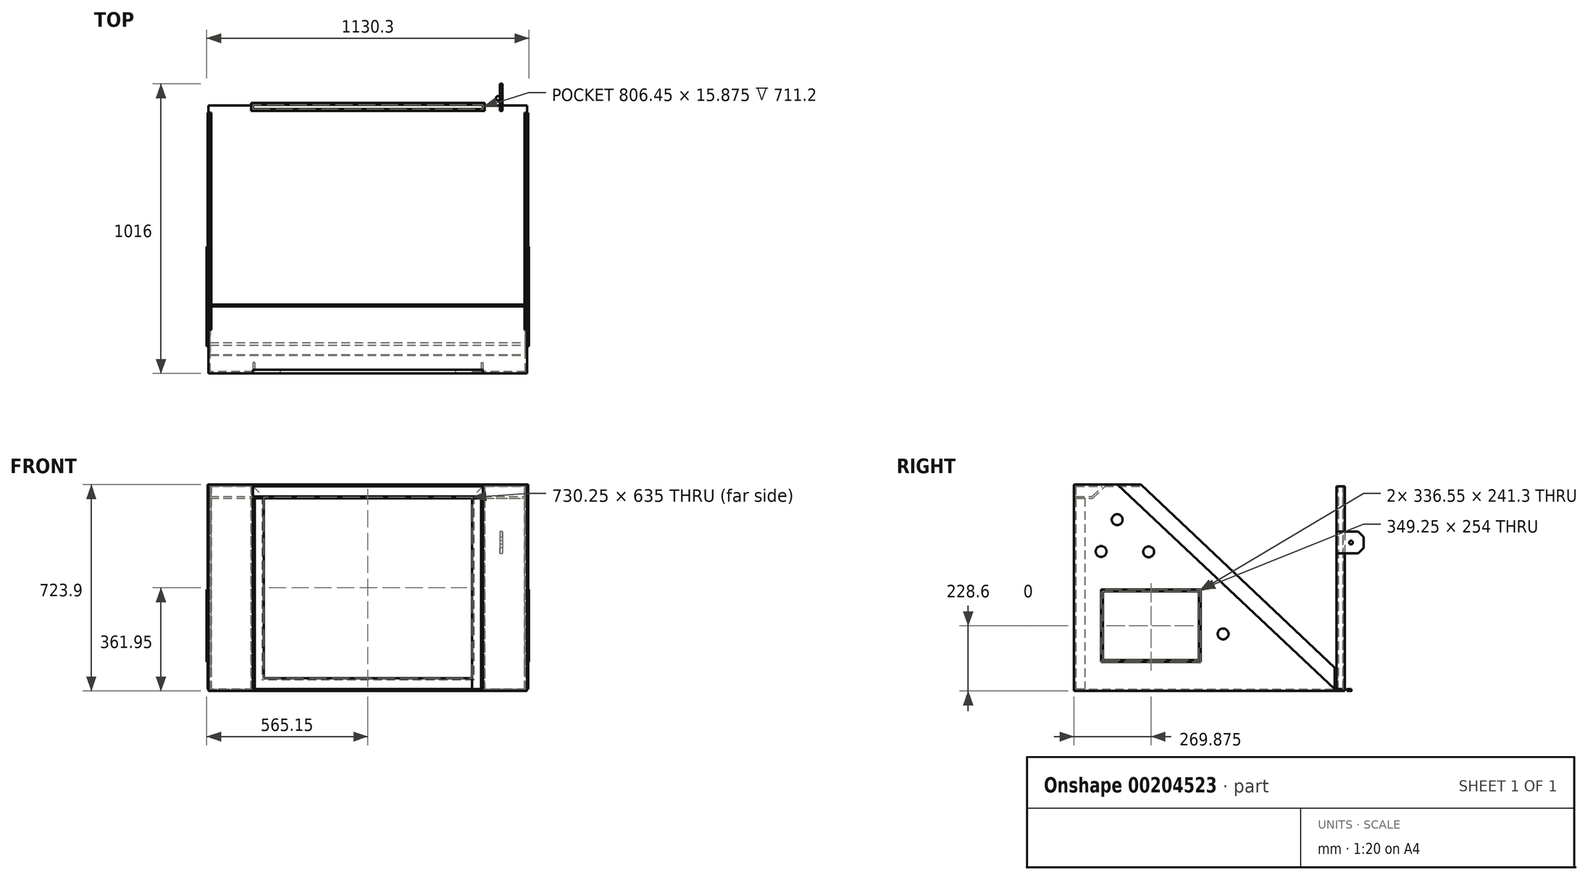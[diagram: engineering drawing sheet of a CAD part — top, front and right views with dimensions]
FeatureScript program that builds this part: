
annotation { "Feature Type Name" : "Feature", "Feature Type Description" : "" }
export const myFeature = defineFeature(function(context is Context, id is Id, definition is map)
    precondition{}
    {
        {
            var Q0;
            Q0=qCreatedBy(makeId("Front.planeOp"),FACE);
            var sketch = newSketch(context, id + "F0", { "sketchPlane" : qUnion([Q0])});
            skLineSegment(sketch, "E0", {"start": v(-558.8, 361.95) * mm, "end": v(-558.8, -361.95) * mm});
            skLineSegment(sketch, "E1", {"start": v(-558.8, -361.95) * mm, "end": v(558.8, -361.95) * mm});
            skLineSegment(sketch, "E2", {"start": v(558.8, -361.95) * mm, "end": v(558.8, 361.95) * mm});
            skLineSegment(sketch, "E3", {"start": v(-558.8, 361.95) * mm, "end": v(558.8, 361.95) * mm});
            skLineSegment(sketch, "E4", {"start": v(-403.23, -355.6) * mm, "end": v(-403.23, 355.6) * mm});
            skLineSegment(sketch, "E5", {"start": v(-403.23, 355.6) * mm, "end": v(403.22, 355.6) * mm});
            skLineSegment(sketch, "E6", {"start": v(403.22, 355.6) * mm, "end": v(403.22, -355.6) * mm});
            skLineSegment(sketch, "E7", {"start": v(-403.22, -355.6) * mm, "end": v(403.22, -355.6) * mm});
            skLineSegment(sketch, "E8", {"start": v(-552.45, 361.95) * mm, "end": v(-552.45, -361.95) * mm});
            skLineSegment(sketch, "E9", {"start": v(552.45, 361.95) * mm, "end": v(552.45, -361.95) * mm});
            skLineSegment(sketch, "E10", {"start": v(403.22, 355.6) * mm, "end": v(552.45, 355.6) * mm});
            skLineSegment(sketch, "E11", {"start": v(-403.23, 355.6) * mm, "end": v(-552.45, 355.6) * mm});
            skLineSegment(sketch, "E12", {"start": v(403.22, -355.6) * mm, "end": v(552.45, -355.6) * mm});
            skLineSegment(sketch, "E13", {"start": v(-403.23, -355.6) * mm, "end": v(-552.45, -355.6) * mm});
            skSolve(sketch);
        }
        {
            var Q0;
            Q0=makeQuery(id+"F0.imprint","IMPRINT",FACE,{"disambiguationData":[TD([[makeQuery(id+"F0.imprint","IMPRINT",EDGE,{"derivedFrom":sQuery(id+"F0.wireOp",EDGE,"E4")}),1.0]])]});
            var Q1;
            Q1=makeQuery(id+"F0.imprint","IMPRINT",FACE,{"disambiguationData":[TD([[makeQuery(id+"F0.imprint","IMPRINT",EDGE,{"derivedFrom":sQuery(id+"F0.wireOp",EDGE,"E6")}),1.0]])]});
            extrude(context, id + "F1", {"entities" : qUnion([Q0, Q1]), "depth" : 6.35 * mm});
        }
        {
            var Q0;
            {var subQ0=sQuery(id+"F0.wireOp",EDGE,"E0");Q0=makeQuery(id+"F0.imprint","IMPRINT",FACE,{"disambiguationData":[TD([[makeQuery(id+"F0.imprint","IMPRINT",EDGE,{"derivedFrom":subQ0}),1.0]])]});}
            var Q1;
            {var subQ0=sQuery(id+"F0.wireOp",EDGE,"E2");Q1=makeQuery(id+"F0.imprint","IMPRINT",FACE,{"disambiguationData":[TD([[makeQuery(id+"F0.imprint","IMPRINT",EDGE,{"derivedFrom":subQ0}),1.0]])]});}
            extrude(context, id + "F2", {"entities" : qUnion([Q0, Q1]), "operationType" : NewBodyOperationType.ADD, "depth" : 914.4 * mm});
        }
        {
            var Q0;
            Q0=makeQuery(id+"F0.imprint","IMPRINT",FACE,{"disambiguationData":[TD([[makeQuery(id+"F0.imprint","IMPRINT",EDGE,{"derivedFrom":sQuery(id+"F0.wireOp",EDGE,"E5")}),1.0]])]});
            var Q1;
            Q1=makeQuery(id+"F0.imprint","IMPRINT",FACE,{"disambiguationData":[TD([[makeQuery(id+"F0.imprint","IMPRINT",EDGE,{"derivedFrom":sQuery(id+"F0.wireOp",EDGE,"E7")}),-1.0]])]});
            extrude(context, id + "F3", {"entities" : qUnion([Q0, Q1]), "operationType" : NewBodyOperationType.ADD, "depth" : 914.4 * mm});
        }
        {
            var Q0;
            {var subQ0=sQuery(id+"F0.wireOp",EDGE,"E9");var subQ1=sQuery(id+"F0.wireOp",EDGE,"E8");var subQ2=sQuery(id+"F0.wireOp",EDGE,"E3");var subQ3=sQuery(id+"F0.wireOp",EDGE,"E1");Q0=makeQuery(id+"F3.boolean.opBoolean","MERGE",FACE,{"derivedFrom":[makeQuery(id+"F2.opExtrude","CAP_FACE",FACE,{"disambiguationData":[OSD([sQuery(id+"F0.wireOp",EDGE,"E0"),subQ3,subQ2,subQ1])],"isStart":false}),makeQuery(id+"F2.opExtrude","CAP_FACE",FACE,{"disambiguationData":[OSD([subQ3,sQuery(id+"F0.wireOp",EDGE,"E2"),subQ2,subQ0])],"isStart":false}),makeQuery(id+"F3.opExtrude","CAP_FACE",FACE,{"disambiguationData":[OSD([subQ3,sQuery(id+"F0.wireOp",EDGE,"E7"),subQ1,subQ0,sQuery(id+"F0.wireOp",EDGE,"E12"),sQuery(id+"F0.wireOp",EDGE,"E13")])],"isStart":false}),makeQuery(id+"F3.opExtrude","CAP_FACE",FACE,{"disambiguationData":[OSD([subQ2,sQuery(id+"F0.wireOp",EDGE,"E5"),subQ1,subQ0,sQuery(id+"F0.wireOp",EDGE,"E10"),sQuery(id+"F0.wireOp",EDGE,"E11")])],"isStart":false})]});}
            var sketch = newSketch(context, id + "F4", { "sketchPlane" : qUnion([Q0])});
            skLineSegment(sketch, "E14.bottom", {"start": v(-558.8, 361.95) * mm, "end": v(558.8, 361.95) * mm});
            skLineSegment(sketch, "E14.top", {"start": v(-558.8, -361.95) * mm, "end": v(558.8, -361.95) * mm});
            skLineSegment(sketch, "E14.left", {"start": v(-558.8, 361.95) * mm, "end": v(-558.8, -361.95) * mm});
            skLineSegment(sketch, "E14.right", {"start": v(558.8, 361.95) * mm, "end": v(558.8, -361.95) * mm});
            skSolve(sketch);
        }
        {
            var Q0;
            Q0=qSketchRegion(id+"F4",true);
            extrude(context, id + "F5", {"entities" : qUnion([Q0]), "operationType" : NewBodyOperationType.ADD, "depth" : 6.35 * mm});
        }
        {
            var Q0;
            Q0=makeQuery(id+"F5.boolean.opBoolean","MERGE",FACE,{"derivedFrom":[makeQuery(id+"F2.opExtrude","SWEPT_FACE",FACE,{"disambiguationData":[OSD([sQuery(id+"F0.wireOp",EDGE,"E2")])]}),makeQuery(id+"F5.opExtrude","SWEPT_FACE",FACE,{"disambiguationData":[OSD([sQuery(id+"F4.wireOp",EDGE,"E14.right")])]})]});
            var sketch = newSketch(context, id + "F6", { "sketchPlane" : qUnion([Q0])});
            skLineSegment(sketch, "E15.bottom", {"start": v(-825.5, -6.35) * mm, "end": v(-476.25, -6.35) * mm});
            skLineSegment(sketch, "E15.top", {"start": v(-825.5, -260.35) * mm, "end": v(-476.25, -260.35) * mm});
            skLineSegment(sketch, "E15.left", {"start": v(-825.5, -6.35) * mm, "end": v(-825.5, -260.35) * mm});
            skLineSegment(sketch, "E15.right", {"start": v(-476.25, -6.35) * mm, "end": v(-476.25, -260.35) * mm});
            skLineSegment(sketch, "E16.0", {"start": v(-819.15, -12.7) * mm, "end": v(-482.6, -12.7) * mm});
            skLineSegment(sketch, "E16.1", {"start": v(-819.15, -12.7) * mm, "end": v(-819.15, -254) * mm});
            skLineSegment(sketch, "E16.2", {"start": v(-819.15, -254) * mm, "end": v(-482.6, -254) * mm});
            skLineSegment(sketch, "E16.3", {"start": v(-482.6, -12.7) * mm, "end": v(-482.6, -254) * mm});
            skSolve(sketch);
        }
        {
            var Q0;
            Q0=makeQuery(id+"F6.imprint","IMPRINT",FACE,{"disambiguationData":[TD([[makeQuery(id+"F6.imprint","IMPRINT",EDGE,{"derivedFrom":sQuery(id+"F6.wireOp",EDGE,"E16.0")}),-1.0]])]});
            extrude(context, id + "F7", {"entities" : qUnion([Q0]), "operationType" : NewBodyOperationType.REMOVE, "oppositeDirection" : true, "depth" : 1270 * mm});
        }
        {
            var Q0;
            Q0=makeQuery(id+"F6.imprint","IMPRINT",FACE,{"disambiguationData":[TD([[makeQuery(id+"F6.imprint","IMPRINT",EDGE,{"derivedFrom":sQuery(id+"F6.wireOp",EDGE,"E15.bottom")}),-1.0]])]});
            extrude(context, id + "F8", {"entities" : qUnion([Q0]), "operationType" : NewBodyOperationType.ADD, "depth" : 6.35 * mm});
        }
        {
            var Q0;
            Q0=makeQuery(id+"F5.boolean.opBoolean","MERGE",FACE,{"derivedFrom":[makeQuery(id+"F2.opExtrude","SWEPT_FACE",FACE,{"disambiguationData":[OSD([sQuery(id+"F0.wireOp",EDGE,"E0")])]}),makeQuery(id+"F5.opExtrude","SWEPT_FACE",FACE,{"disambiguationData":[OSD([sQuery(id+"F4.wireOp",EDGE,"E14.left")])]})]});
            var sketch = newSketch(context, id + "F9", { "sketchPlane" : qUnion([Q0])});
            skLineSegment(sketch, "E17.0", {"start": v(825.5, -6.35) * mm, "end": v(476.25, -6.35) * mm});
            skLineSegment(sketch, "E17.1", {"start": v(825.5, -6.35) * mm, "end": v(825.5, -260.35) * mm});
            skLineSegment(sketch, "E17.2", {"start": v(825.5, -260.35) * mm, "end": v(476.25, -260.35) * mm});
            skLineSegment(sketch, "E17.3", {"start": v(476.25, -6.35) * mm, "end": v(476.25, -260.35) * mm});
            skSolve(sketch);
        }
        {
            var Q0;
            Q0=makeQuery(id+"F9.imprint","IMPRINT",FACE,{"disambiguationData":[TD([[makeQuery(id+"F9.imprint","IMPRINT",EDGE,{"derivedFrom":sQuery(id+"F9.wireOp",EDGE,"E17.0")}),1.0]])]});
            extrude(context, id + "F10", {"entities" : qUnion([Q0]), "operationType" : NewBodyOperationType.ADD, "depth" : 6.35 * mm});
        }
        {
            var Q0;
            Q0=makeQuery(id+"F5.boolean.opBoolean","MERGE",FACE,{"derivedFrom":[makeQuery(id+"F2.opExtrude","SWEPT_FACE",FACE,{"disambiguationData":[OSD([sQuery(id+"F0.wireOp",EDGE,"E0")])]}),makeQuery(id+"F5.opExtrude","SWEPT_FACE",FACE,{"disambiguationData":[OSD([sQuery(id+"F4.wireOp",EDGE,"E14.left")])]})]});
            var sketch = newSketch(context, id + "F11", { "sketchPlane" : qUnion([Q0])});
            skCircle(sketch, "E18.5.0.0", {"center": v(769.22, 239.06) * mm, "radius": 19.05 * mm});
            skCircle(sketch, "E19.3.0.0", {"center": v(658.89, 126.27) * mm, "radius": 19.05 * mm});
            skCircle(sketch, "E19.4.0.0", {"center": v(825.62, 127.5) * mm, "radius": 19.05 * mm});
            skCircle(sketch, "E20.MirrorC", {"center": v(397.76, -161.83) * mm, "radius": 19.05 * mm});
            skLineSegment(sketch, "E21", {"start": v(920.75, 361.95) * mm, "end": v(768.35, 361.95) * mm});
            skLineSegment(sketch, "E22", {"start": v(768.35, 361.95) * mm, "end": v(685.8, 361.95) * mm});
            skLineSegment(sketch, "E23", {"start": v(0, -361.95) * mm, "end": v(0, -285.75) * mm});
            skLineSegment(sketch, "E24", {"start": v(6.35, -279.75) * mm, "end": v(685.8, 361.95) * mm});
            skLineSegment(sketch, "E25", {"start": v(685.8, 361.95) * mm, "end": v(0, 361.95) * mm});
            skLineSegment(sketch, "E26", {"start": v(0, 361.95) * mm, "end": v(0, -285.75) * mm});
            skLineSegment(sketch, "E27", {"start": v(6.35, -361.95) * mm, "end": v(6.35, -279.75) * mm});
            skLineSegment(sketch, "E28", {"start": v(768.35, 361.95) * mm, "end": v(768.35, 336.55) * mm});
            skLineSegment(sketch, "E29", {"start": v(768.35, 336.55) * mm, "end": v(28.76, -361.95) * mm});
            skLineSegment(sketch, "E30", {"start": v(28.76, -361.95) * mm, "end": v(6.35, -361.95) * mm});
            skSolve(sketch);
        }
        {
            var Q0;
            Q0=sQuery(id+"F11.wireOp",VERTEX,"E18.direction1.start");
            var Q1;
            Q1=sQuery(id+"F11.wireOp",VERTEX,"E19.direction1.start");
            var Q2;
            Q2=sQuery(id+"F11.wireOp",VERTEX,"4a2ce049-4093-4add-8b6f-b7f52deebb400.MirrorC.center");
            var Q3;
            Q3=sQuery(id+"F11.wireOp",VERTEX,"a850cc24-eb14-4aa5-b13c-ffba9507b1460.MirrorC.center");
            var Q4;
            Q4=sQuery(id+"F11.wireOp",VERTEX,"E20.MirrorC.center");
            var Q5;
            Q5=sQuery(id+"F11.wireOp",VERTEX,"a32a4dfc-9795-497b-a0e1-e86128ed9b480.MirrorC.center");
            var Q6;
            Q6=sQuery(id+"F11.wireOp",VERTEX,"E19.direction1.end");
            var Q7;
            Q7=sQuery(id+"F11.wireOp",VERTEX,"E18.direction1.end");
            var Q8;
            Q8=sQuery(id+"F11.wireOp",VERTEX,"E18.2.0.0.center");
            var Q9;
            Q9=sQuery(id+"F11.wireOp",VERTEX,"E18.3.0.0.center");
            var Q10;
            Q10=sQuery(id+"F11.wireOp",VERTEX,"E19.3.0.0.center");
            var Q11;
            Q11=sQuery(id+"F11.wireOp",VERTEX,"E19.2.0.0.center");
            var Q12;
            Q12=sQuery(id+"F11.wireOp",VERTEX,"E18.4.0.0.center");
            var Q13;
            Q13=sQuery(id+"F11.wireOp",VERTEX,"E19.4.0.0.center");
            var Q14;
            Q14=sQuery(id+"F11.wireOp",VERTEX,"E18.5.0.0.center");
            var Q15;
            Q15=makeQuery(id+"F1.opExtrude","SWEPT_BODY",BODY,{"disambiguationData":[OSD([sQuery(id+"F0.wireOp",EDGE,"E4"),sQuery(id+"F0.wireOp",EDGE,"E8"),sQuery(id+"F0.wireOp",EDGE,"E11"),sQuery(id+"F0.wireOp",EDGE,"E13")])]});
            hole(context, id + "F12", {"style" : HoleStyle.SIMPLE, "endStyle" : HoleEndStyle.BLIND, "holeDiameter" : 38.1 * mm, "holeDepth" : 1524 * mm, "locations" : qUnion([Q0, Q1, Q2, Q3, Q4, Q5, Q6, Q7, Q8, Q9, Q10, Q11, Q12, Q13, Q14]), "scope" : qUnion([Q15])});
        }
        {
            var Q0;
            {var subQ0=sQuery(id+"F0.wireOp",EDGE,"E3");Q0=makeQuery(id+"F5.boolean.opBoolean","MERGE",FACE,{"derivedFrom":[makeQuery(id+"F3.boolean.opBoolean","MERGE",FACE,{"derivedFrom":[makeQuery(id+"F2.opExtrude","SWEPT_FACE",FACE,{"disambiguationData":[OSD([subQ0]),TDD([makeQuery(id+"F0.imprint","IMPRINT",EDGE,{"disambiguationData":[TD([[makeQuery(id+"F0.imprint","INTERSECT",VERTEX,{"derivedFrom":[sQuery(id+"F0.wireOp",EDGE,"E0"),subQ0]}),-1.0]])],"derivedFrom":subQ0})])]}),makeQuery(id+"F2.opExtrude","SWEPT_FACE",FACE,{"disambiguationData":[OSD([subQ0]),TDD([makeQuery(id+"F0.imprint","IMPRINT",EDGE,{"disambiguationData":[TD([[makeQuery(id+"F0.imprint","INTERSECT",VERTEX,{"derivedFrom":[sQuery(id+"F0.wireOp",EDGE,"E2"),subQ0]}),1.0]])],"derivedFrom":subQ0})])]}),makeQuery(id+"F3.opExtrude","SWEPT_FACE",FACE,{"disambiguationData":[OSD([subQ0])]})]}),makeQuery(id+"F5.opExtrude","SWEPT_FACE",FACE,{"disambiguationData":[OSD([sQuery(id+"F4.wireOp",EDGE,"E14.bottom")])]})]});}
            var sketch = newSketch(context, id + "F13", { "sketchPlane" : qUnion([Q0])});
            skLineSegment(sketch, "E31", {"start": v(188.2, -141.31) * mm, "end": v(366, -141.31) * mm});
            skLineSegment(sketch, "E32", {"start": v(366, -141.31) * mm, "end": v(366, -382.61) * mm});
            skLineSegment(sketch, "E33", {"start": v(366, -382.61) * mm, "end": v(188.2, -382.61) * mm});
            skLineSegment(sketch, "E34", {"start": v(188.2, -382.61) * mm, "end": v(188.2, -141.31) * mm});
            skSolve(sketch);
        }
        {
            var Q0;
            Q0=makeQuery(id+"F13.imprint","IMPRINT",FACE,{"disambiguationData":[TD([[makeQuery(id+"F13.imprint","IMPRINT",EDGE,{"derivedFrom":sQuery(id+"F13.wireOp",EDGE,"E31")}),-1.0]])]});
            extrude(context, id + "F14", {"entities" : qUnion([Q0]), "operationType" : NewBodyOperationType.REMOVE, "oppositeDirection" : true, "depth" : 25.4 * mm});
        }
        {
            var Q0;
            Q0=makeQuery(id+"F0.imprint","IMPRINT",FACE,{"disambiguationData":[TD([[makeQuery(id+"F0.imprint","IMPRINT",EDGE,{"derivedFrom":sQuery(id+"F0.wireOp",EDGE,"E6")}),1.0]])]});
            var sketch = newSketch(context, id + "F15", { "sketchPlane" : qUnion([Q0])});
            skLineSegment(sketch, "E35.bottom", {"start": v(472.25, 196.85) * mm, "end": v(462.72, 196.85) * mm});
            skLineSegment(sketch, "E35.top", {"start": v(472.25, 120.65) * mm, "end": v(462.72, 120.65) * mm});
            skLineSegment(sketch, "E35.left", {"start": v(472.25, 196.85) * mm, "end": v(472.25, 120.65) * mm});
            skLineSegment(sketch, "E35.right", {"start": v(462.72, 196.85) * mm, "end": v(462.72, 120.65) * mm});
            skSolve(sketch);
        }
        {
            var Q0;
            Q0=qSketchRegion(id+"F15",true);
            extrude(context, id + "F16", {"entities" : qUnion([Q0]), "operationType" : NewBodyOperationType.ADD, "oppositeDirection" : true, "depth" : 95.25 * mm});
        }
        {
            var Q0;
            Q0=makeQuery(id+"F16.opExtrude","CAP_EDGE",EDGE,{"disambiguationData":[OSD([sQuery(id+"F15.wireOp",EDGE,"E35.top")])],"isStart":false});
            var Q1;
            Q1=makeQuery(id+"F16.opExtrude","CAP_EDGE",EDGE,{"disambiguationData":[OSD([sQuery(id+"F15.wireOp",EDGE,"E35.bottom")])],"isStart":false});
            chamfer(context, id + "F17", {"entities" : qUnion([Q0, Q1]), "width" : 19.05 * mm, "tangentPropagation" : true});
        }
        {
            var Q0;
            Q0=makeQuery(id+"F16.opExtrude","SWEPT_FACE",FACE,{"disambiguationData":[OSD([sQuery(id+"F15.wireOp",EDGE,"E35.right")])]});
            var sketch = newSketch(context, id + "F18", { "sketchPlane" : qUnion([Q0])});
            skLineSegment(sketch, "E36", {"start": v(-50.8, 120.65) * mm, "end": v(-50.8, 158.75) * mm});
            skSolve(sketch);
        }
        {
            var Q0;
            Q0=sQuery(id+"F18.wireOp",VERTEX,"E36.end");
            var Q1;
            Q1=makeQuery(id+"F1.opExtrude","SWEPT_BODY",BODY,{"disambiguationData":[OSD([sQuery(id+"F0.wireOp",EDGE,"E4"),sQuery(id+"F0.wireOp",EDGE,"E8"),sQuery(id+"F0.wireOp",EDGE,"E11"),sQuery(id+"F0.wireOp",EDGE,"E13")])]});
            hole(context, id + "F19", {"style" : HoleStyle.SIMPLE, "endStyle" : HoleEndStyle.BLIND, "holeDiameter" : 12.7 * mm, "holeDepth" : 1524 * mm, "locations" : qUnion([Q0]), "scope" : qUnion([Q1])});
        }
        {
            var Q0;
            Q0=makeQuery(id+"F0.imprint","IMPRINT",FACE,{"disambiguationData":[TD([[makeQuery(id+"F0.imprint","IMPRINT",EDGE,{"derivedFrom":sQuery(id+"F0.wireOp",EDGE,"E4")}),-1.0]])]});
            extrude(context, id + "F20", {"entities" : qUnion([Q0]), "operationType" : NewBodyOperationType.REMOVE, "depth" : 1270 * mm});
        }
        {
            var Q0;
            Q0=makeQuery(id+"F0.imprint","IMPRINT",FACE,{"disambiguationData":[TD([[makeQuery(id+"F0.imprint","IMPRINT",EDGE,{"derivedFrom":sQuery(id+"F0.wireOp",EDGE,"E4")}),-1.0]])]});
            var sketch = newSketch(context, id + "F21", { "sketchPlane" : qUnion([Q0])});
            skLineSegment(sketch, "E37", {"start": v(403.23, 355.6) * mm, "end": v(403.23, -355.6) * mm});
            skLineSegment(sketch, "E38.0", {"start": v(365.13, 317.5) * mm, "end": v(365.13, -317.5) * mm});
            skLineSegment(sketch, "E39", {"start": v(403.23, 355.6) * mm, "end": v(365.13, 317.5) * mm});
            skLineSegment(sketch, "E40", {"start": v(403.23, -355.6) * mm, "end": v(365.13, -317.5) * mm});
            skLineSegment(sketch, "E41.0", {"start": v(396.88, 349.25) * mm, "end": v(396.88, -349.25) * mm});
            skLineSegment(sketch, "E42.MirrorCS", {"start": v(-365.13, 317.5) * mm, "end": v(-365.13, -317.5) * mm});
            skLineSegment(sketch, "E43.MirrorCS", {"start": v(-396.88, 349.25) * mm, "end": v(-396.88, -349.25) * mm});
            skLineSegment(sketch, "E44.MirrorCS", {"start": v(-403.23, 355.6) * mm, "end": v(-403.23, -355.6) * mm});
            skLineSegment(sketch, "E45.MirrorCS", {"start": v(-403.23, 355.6) * mm, "end": v(-365.13, 317.5) * mm});
            skLineSegment(sketch, "E46.MirrorCS", {"start": v(-403.23, -355.6) * mm, "end": v(-365.13, -317.5) * mm});
            skLineSegment(sketch, "E47", {"start": v(403.23, 355.6) * mm, "end": v(-403.23, 355.6) * mm});
            skLineSegment(sketch, "E48", {"start": v(365.13, 317.5) * mm, "end": v(-365.13, 317.5) * mm});
            skLineSegment(sketch, "E49", {"start": v(-396.88, 349.25) * mm, "end": v(396.88, 349.25) * mm});
            skLineSegment(sketch, "E50.MirrorCS", {"start": v(365.13, -317.5) * mm, "end": v(-365.13, -317.5) * mm});
            skLineSegment(sketch, "E51.MirrorCS", {"start": v(-396.88, -349.25) * mm, "end": v(396.88, -349.25) * mm});
            skLineSegment(sketch, "E52.MirrorCS", {"start": v(403.23, -355.6) * mm, "end": v(-403.23, -355.6) * mm});
            skSolve(sketch);
        }
        {
            var Q0;
            {var subQ0=sQuery(id+"F21.wireOp",EDGE,"E42.MirrorCS");Q0=makeQuery(id+"F21.imprint","IMPRINT",FACE,{"disambiguationData":[TD([[makeQuery(id+"F21.imprint","IMPRINT",EDGE,{"derivedFrom":subQ0}),-1.0]])]});}
            var Q1;
            {var subQ0=sQuery(id+"F21.wireOp",EDGE,"E48");Q1=makeQuery(id+"F21.imprint","IMPRINT",FACE,{"disambiguationData":[TD([[makeQuery(id+"F21.imprint","IMPRINT",EDGE,{"derivedFrom":subQ0}),-1.0]])]});}
            var Q2;
            {var subQ0=sQuery(id+"F21.wireOp",EDGE,"E50.MirrorCS");Q2=makeQuery(id+"F21.imprint","IMPRINT",FACE,{"disambiguationData":[TD([[makeQuery(id+"F21.imprint","IMPRINT",EDGE,{"derivedFrom":subQ0}),1.0]])]});}
            var Q3;
            {var subQ0=sQuery(id+"F21.wireOp",EDGE,"E38.0");Q3=makeQuery(id+"F21.imprint","IMPRINT",FACE,{"disambiguationData":[TD([[makeQuery(id+"F21.imprint","IMPRINT",EDGE,{"derivedFrom":subQ0}),1.0]])]});}
            extrude(context, id + "F22", {"entities" : qUnion([Q0, Q1, Q2, Q3]), "oppositeDirection" : true, "depth" : 6.35 * mm});
        }
        {
            var Q0;
            {var subQ0=sQuery(id+"F21.wireOp",EDGE,"E47");Q0=makeQuery(id+"F21.imprint","IMPRINT",FACE,{"disambiguationData":[TD([[makeQuery(id+"F21.imprint","IMPRINT",EDGE,{"derivedFrom":subQ0}),-1.0]])]});}
            var Q1;
            {var subQ0=sQuery(id+"F21.wireOp",EDGE,"E37");Q1=makeQuery(id+"F21.imprint","IMPRINT",FACE,{"disambiguationData":[TD([[makeQuery(id+"F21.imprint","IMPRINT",EDGE,{"derivedFrom":subQ0}),-1.0]])]});}
            var Q2;
            {var subQ2=sQuery(id+"F21.wireOp",EDGE,"E51.MirrorCS");Q2=makeQuery(id+"F21.imprint","IMPRINT",FACE,{"disambiguationData":[TD([[makeQuery(id+"F21.imprint","IMPRINT",EDGE,{"derivedFrom":subQ2}),-1.0]])]});}
            var Q3;
            {var subQ0=sQuery(id+"F21.wireOp",EDGE,"E43.MirrorCS");Q3=makeQuery(id+"F21.imprint","IMPRINT",FACE,{"disambiguationData":[TD([[makeQuery(id+"F21.imprint","IMPRINT",EDGE,{"derivedFrom":subQ0}),-1.0]])]});}
            var Q4;
            Q4=makeQuery(id+"F22.opExtrude","CAP_FACE",FACE,{"disambiguationData":[OSD([sQuery(id+"F21.wireOp",EDGE,"E38.0"),sQuery(id+"F21.wireOp",EDGE,"E41.0"),sQuery(id+"F21.wireOp",EDGE,"E42.MirrorCS"),sQuery(id+"F21.wireOp",EDGE,"E43.MirrorCS"),sQuery(id+"F21.wireOp",EDGE,"E48"),sQuery(id+"F21.wireOp",EDGE,"E49"),sQuery(id+"F21.wireOp",EDGE,"E50.MirrorCS"),sQuery(id+"F21.wireOp",EDGE,"E51.MirrorCS")])],"isStart":false});
            extrude(context, id + "F23", {"entities" : qUnion([Q0, Q1, Q2, Q3]), "depth" : 25.4 * mm, "hasSecondDirection" : true, "secondDirectionBound" : SecondDirectionBoundingType.UP_TO_SURFACE, "secondDirectionOppositeDirection" : true, "secondDirectionBoundEntityFace" : qUnion([Q4]), "secondDirectionDepth" : 25.4 * mm});
        }
        {
            var Q0;
            Q0=makeQuery(id+"F22.opExtrude","SWEPT_BODY",BODY,{"disambiguationData":[OSD([sQuery(id+"F21.wireOp",EDGE,"E38.0"),sQuery(id+"F21.wireOp",EDGE,"E41.0"),sQuery(id+"F21.wireOp",EDGE,"E42.MirrorCS"),sQuery(id+"F21.wireOp",EDGE,"E43.MirrorCS"),sQuery(id+"F21.wireOp",EDGE,"E48"),sQuery(id+"F21.wireOp",EDGE,"E49"),sQuery(id+"F21.wireOp",EDGE,"E50.MirrorCS"),sQuery(id+"F21.wireOp",EDGE,"E51.MirrorCS")])]});
            var Q1;
            Q1=makeQuery(id+"F23.opExtrude","SWEPT_BODY",BODY,{"disambiguationData":[OSD([sQuery(id+"F21.wireOp",EDGE,"E37"),sQuery(id+"F21.wireOp",EDGE,"E41.0"),sQuery(id+"F21.wireOp",EDGE,"E43.MirrorCS"),sQuery(id+"F21.wireOp",EDGE,"E44.MirrorCS"),sQuery(id+"F21.wireOp",EDGE,"E47"),sQuery(id+"F21.wireOp",EDGE,"E49"),sQuery(id+"F21.wireOp",EDGE,"E51.MirrorCS"),sQuery(id+"F21.wireOp",EDGE,"E52.MirrorCS")])]});
            var Q2;
            Q2=makeQuery(id+"F1.opExtrude","SWEPT_BODY",BODY,{"disambiguationData":[OSD([sQuery(id+"F0.wireOp",EDGE,"E4"),sQuery(id+"F0.wireOp",EDGE,"E8"),sQuery(id+"F0.wireOp",EDGE,"E11"),sQuery(id+"F0.wireOp",EDGE,"E13")])]});
            booleanBodies(context, id + "F24", {"operationType" : BooleanOperationType.UNION, "tools" : qUnion([Q0, Q1, Q2])});
        }
        {
            var Q0;
            {var subQ0=sQuery(id+"F21.wireOp",EDGE,"E51.MirrorCS");var subQ1=sQuery(id+"F21.wireOp",EDGE,"E49");var subQ2=sQuery(id+"F21.wireOp",EDGE,"E43.MirrorCS");var subQ3=sQuery(id+"F21.wireOp",EDGE,"E41.0");Q0=makeQuery(id+"F24.opBoolean","MERGE",FACE,{"derivedFrom":[makeQuery(id+"F22.opExtrude","CAP_FACE",FACE,{"disambiguationData":[OSD([sQuery(id+"F21.wireOp",EDGE,"E38.0"),subQ3,sQuery(id+"F21.wireOp",EDGE,"E42.MirrorCS"),subQ2,sQuery(id+"F21.wireOp",EDGE,"E48"),subQ1,sQuery(id+"F21.wireOp",EDGE,"E50.MirrorCS"),subQ0])],"isStart":false}),makeQuery(id+"F23.opExtrude","CAP_FACE",FACE,{"disambiguationData":[OSD([sQuery(id+"F21.wireOp",EDGE,"E37"),subQ3,subQ2,sQuery(id+"F21.wireOp",EDGE,"E44.MirrorCS"),sQuery(id+"F21.wireOp",EDGE,"E47"),subQ1,subQ0,sQuery(id+"F21.wireOp",EDGE,"E52.MirrorCS")])],"isStart":true})]});}
            var sketch = newSketch(context, id + "F25", { "sketchPlane" : qUnion([Q0])});
            skLineSegment(sketch, "E53.0", {"start": v(371.48, 324.21) * mm, "end": v(371.48, -323.85) * mm});
            skLineSegment(sketch, "E53.1", {"start": v(-371.48, -323.85) * mm, "end": v(371.48, -323.85) * mm});
            skLineSegment(sketch, "E53.2", {"start": v(-371.48, 324.21) * mm, "end": v(-371.48, -323.85) * mm});
            skLineSegment(sketch, "E54.MirrorCS", {"start": v(403.22, 355.6) * mm, "end": v(371.48, 324.21) * mm});
            skLineSegment(sketch, "E55.0", {"start": v(403.23, 355.6) * mm, "end": v(403.23, -355.6) * mm});
            skLineSegment(sketch, "E55.1", {"start": v(-403.23, -355.6) * mm, "end": v(403.23, -355.6) * mm});
            skLineSegment(sketch, "E55.2", {"start": v(-403.23, 355.64) * mm, "end": v(-403.23, -355.6) * mm});
            skLineSegment(sketch, "E56", {"start": v(-403.23, 355.64) * mm, "end": v(-371.48, 324.21) * mm});
            skLineSegment(sketch, "E57.0", {"start": v(409.58, 355.6) * mm, "end": v(409.58, -361.95) * mm});
            skLineSegment(sketch, "E57.1", {"start": v(-409.58, -361.95) * mm, "end": v(409.58, -361.95) * mm});
            skLineSegment(sketch, "E57.2", {"start": v(-409.58, 355.6) * mm, "end": v(-409.58, -361.95) * mm});
            skLineSegment(sketch, "E58", {"start": v(-403.23, 355.64) * mm, "end": v(-409.58, 355.6) * mm});
            skLineSegment(sketch, "E59", {"start": v(403.22, 355.6) * mm, "end": v(409.58, 355.6) * mm});
            skSolve(sketch);
        }
        {
            var Q0;
            Q0=makeQuery(id+"F25.imprint","IMPRINT",FACE,{"disambiguationData":[TD([[makeQuery(id+"F25.imprint","IMPRINT",EDGE,{"derivedFrom":sQuery(id+"F25.wireOp",EDGE,"E53.0")}),1.0]])]});
            extrude(context, id + "F26", {"entities" : qUnion([Q0]), "depth" : 22.22 * mm, "hasSecondDirection" : true, "secondDirectionOppositeDirection" : false, "secondDirectionDepth" : 15.88 * mm});
        }
        {
            var Q0;
            Q0=makeQuery(id+"F25.imprint","IMPRINT",FACE,{"disambiguationData":[TD([[makeQuery(id+"F25.imprint","IMPRINT",EDGE,{"derivedFrom":sQuery(id+"F25.wireOp",EDGE,"E55.0")}),-1.0]])]});
            var Q1;
            Q1=makeQuery(id+"F26.opExtrude","CAP_FACE",FACE,{"disambiguationData":[OSD([sQuery(id+"F21.wireOp",EDGE,"E38.0"),sQuery(id+"F21.wireOp",EDGE,"E41.0"),sQuery(id+"F21.wireOp",EDGE,"E42.MirrorCS"),sQuery(id+"F21.wireOp",EDGE,"E43.MirrorCS"),sQuery(id+"F21.wireOp",EDGE,"E47"),sQuery(id+"F21.wireOp",EDGE,"E48"),sQuery(id+"F21.wireOp",EDGE,"E49"),sQuery(id+"F21.wireOp",EDGE,"E50.MirrorCS"),sQuery(id+"F21.wireOp",EDGE,"E51.MirrorCS"),sQuery(id+"F25.wireOp",EDGE,"E53.0"),sQuery(id+"F25.wireOp",EDGE,"E53.1"),sQuery(id+"F25.wireOp",EDGE,"E53.2"),sQuery(id+"F25.wireOp",EDGE,"E54.MirrorCS"),sQuery(id+"F25.wireOp",EDGE,"E55.0"),sQuery(id+"F25.wireOp",EDGE,"E55.1"),sQuery(id+"F25.wireOp",EDGE,"E55.2"),sQuery(id+"F25.wireOp",EDGE,"E56")])],"isStart":false});
            var Q2;
            {var subQ0=sQuery(id+"F0.wireOp",EDGE,"E11");var subQ1=sQuery(id+"F0.wireOp",EDGE,"E10");var subQ2=sQuery(id+"F0.wireOp",EDGE,"E9");var subQ3=sQuery(id+"F0.wireOp",EDGE,"E8");var subQ4=sQuery(id+"F0.wireOp",EDGE,"E3");var subQ5=sQuery(id+"F0.wireOp",EDGE,"E13");var subQ6=sQuery(id+"F0.wireOp",EDGE,"E12");var subQ7=sQuery(id+"F0.wireOp",EDGE,"E1");Q2=makeQuery(id+"F3.boolean.opBoolean","MERGE",FACE,{"derivedFrom":[makeQuery(id+"F2.boolean.opBoolean","MERGE",FACE,{"derivedFrom":[makeQuery(id+"F1.opExtrude","CAP_FACE",FACE,{"disambiguationData":[OSD([sQuery(id+"F0.wireOp",EDGE,"E4"),subQ3,subQ0,subQ5])],"isStart":true}),makeQuery(id+"F2.opExtrude","CAP_FACE",FACE,{"disambiguationData":[OSD([sQuery(id+"F0.wireOp",EDGE,"E0"),subQ7,subQ4,subQ3])],"isStart":true})]}),makeQuery(id+"F2.boolean.opBoolean","MERGE",FACE,{"derivedFrom":[makeQuery(id+"F1.opExtrude","CAP_FACE",FACE,{"disambiguationData":[OSD([sQuery(id+"F0.wireOp",EDGE,"E6"),subQ2,subQ1,subQ6])],"isStart":true}),makeQuery(id+"F2.opExtrude","CAP_FACE",FACE,{"disambiguationData":[OSD([subQ7,sQuery(id+"F0.wireOp",EDGE,"E2"),subQ4,subQ2])],"isStart":true})]}),makeQuery(id+"F3.opExtrude","CAP_FACE",FACE,{"disambiguationData":[OSD([subQ7,sQuery(id+"F0.wireOp",EDGE,"E7"),subQ3,subQ2,subQ6,subQ5])],"isStart":true}),makeQuery(id+"F3.opExtrude","CAP_FACE",FACE,{"disambiguationData":[OSD([subQ4,sQuery(id+"F0.wireOp",EDGE,"E5"),subQ3,subQ2,subQ1,subQ0])],"isStart":true})]});}
            extrude(context, id + "F27", {"entities" : qUnion([Q0]), "operationType" : NewBodyOperationType.ADD, "endBound" : BoundingType.UP_TO_SURFACE, "endBoundEntityFace" : qUnion([Q1]), "depth" : 25.4 * mm, "hasSecondDirection" : true, "secondDirectionBound" : SecondDirectionBoundingType.UP_TO_SURFACE, "secondDirectionOppositeDirection" : true, "secondDirectionBoundEntityFace" : qUnion([Q2]), "secondDirectionDepth" : 25.4 * mm});
        }
        {
            var Q0;
            {var subQ0=sQuery(id+"F0.wireOp",EDGE,"E1");Q0=makeQuery(id+"F5.boolean.opBoolean","MERGE",FACE,{"derivedFrom":[makeQuery(id+"F3.boolean.opBoolean","MERGE",FACE,{"derivedFrom":[makeQuery(id+"F2.opExtrude","SWEPT_FACE",FACE,{"disambiguationData":[OSD([subQ0]),TDD([makeQuery(id+"F0.imprint","IMPRINT",EDGE,{"disambiguationData":[TD([[makeQuery(id+"F0.imprint","INTERSECT",VERTEX,{"derivedFrom":[sQuery(id+"F0.wireOp",EDGE,"E0"),subQ0]}),-1.0]])],"derivedFrom":subQ0})])]}),makeQuery(id+"F2.opExtrude","SWEPT_FACE",FACE,{"disambiguationData":[OSD([subQ0]),TDD([makeQuery(id+"F0.imprint","IMPRINT",EDGE,{"disambiguationData":[TD([[makeQuery(id+"F0.imprint","INTERSECT",VERTEX,{"derivedFrom":[subQ0,sQuery(id+"F0.wireOp",EDGE,"E2")]}),1.0]])],"derivedFrom":subQ0})])]}),makeQuery(id+"F3.opExtrude","SWEPT_FACE",FACE,{"disambiguationData":[OSD([subQ0])]})]}),makeQuery(id+"F5.opExtrude","SWEPT_FACE",FACE,{"disambiguationData":[OSD([sQuery(id+"F4.wireOp",EDGE,"E14.top")])]})]});}
            var sketch = newSketch(context, id + "F28", { "sketchPlane" : qUnion([Q0])});
            skLineSegment(sketch, "E60", {"start": v(0, 920.75) * mm, "end": v(0, 908.05) * mm});
            skPoint(sketch, "E60.endSnap0", {"position": v(0, 920.75) * mm});
            skLineSegment(sketch, "E61", {"start": v(0, 908.05) * mm, "end": v(-307.98, 908.05) * mm});
            skLineSegment(sketch, "E62", {"start": v(-307.98, 908.05) * mm, "end": v(-307.98, 920.75) * mm});
            skLineSegment(sketch, "E63", {"start": v(-307.98, 920.75) * mm, "end": v(307.98, 920.75) * mm});
            skLineSegment(sketch, "E64", {"start": v(307.98, 920.75) * mm, "end": v(307.98, 908.05) * mm});
            skLineSegment(sketch, "E65", {"start": v(307.98, 908.05) * mm, "end": v(0, 908.05) * mm});
            skSolve(sketch);
        }
        {
            var Q0;
            Q0=qSketchRegion(id+"F28",true);
            extrude(context, id + "F29", {"entities" : qUnion([Q0]), "operationType" : NewBodyOperationType.REMOVE, "oppositeDirection" : true, "depth" : 1524 * mm});
        }
        {
            var Q0;
            {var subQ0=sQuery(id+"F0.wireOp",EDGE,"E3");Q0=makeQuery(id+"F5.boolean.opBoolean","MERGE",FACE,{"derivedFrom":[makeQuery(id+"F3.boolean.opBoolean","MERGE",FACE,{"derivedFrom":[makeQuery(id+"F2.opExtrude","SWEPT_FACE",FACE,{"disambiguationData":[OSD([subQ0]),TDD([makeQuery(id+"F0.imprint","IMPRINT",EDGE,{"disambiguationData":[TD([[makeQuery(id+"F0.imprint","INTERSECT",VERTEX,{"derivedFrom":[sQuery(id+"F0.wireOp",EDGE,"E0"),subQ0]}),-1.0]])],"derivedFrom":subQ0})])]}),makeQuery(id+"F2.opExtrude","SWEPT_FACE",FACE,{"disambiguationData":[OSD([subQ0]),TDD([makeQuery(id+"F0.imprint","IMPRINT",EDGE,{"disambiguationData":[TD([[makeQuery(id+"F0.imprint","INTERSECT",VERTEX,{"derivedFrom":[sQuery(id+"F0.wireOp",EDGE,"E2"),subQ0]}),1.0]])],"derivedFrom":subQ0})])]}),makeQuery(id+"F3.opExtrude","SWEPT_FACE",FACE,{"disambiguationData":[OSD([subQ0])]})]}),makeQuery(id+"F5.opExtrude","SWEPT_FACE",FACE,{"disambiguationData":[OSD([sQuery(id+"F4.wireOp",EDGE,"E14.bottom")])]})]});}
            var sketch = newSketch(context, id + "F30", { "sketchPlane" : qUnion([Q0])});
            skLineSegment(sketch, "E66", {"start": v(-307.98, -920.75) * mm, "end": v(-403.22, -920.75) * mm});
            skLineSegment(sketch, "E67", {"start": v(-403.22, -920.75) * mm, "end": v(-403.22, -908.05) * mm});
            skLineSegment(sketch, "E68", {"start": v(-403.22, -908.05) * mm, "end": v(-307.97, -908.05) * mm});
            skLineSegment(sketch, "E69", {"start": v(-307.97, -908.05) * mm, "end": v(-307.97, -920.75) * mm});
            skLineSegment(sketch, "E70", {"start": v(307.98, -908.05) * mm, "end": v(403.23, -908.05) * mm});
            skLineSegment(sketch, "E71", {"start": v(403.23, -908.05) * mm, "end": v(403.23, -920.75) * mm});
            skLineSegment(sketch, "E72", {"start": v(403.23, -920.75) * mm, "end": v(307.98, -920.75) * mm});
            skLineSegment(sketch, "E73", {"start": v(307.98, -920.75) * mm, "end": v(307.98, -908.05) * mm});
            skSolve(sketch);
        }
        {
            var Q0;
            Q0=makeQuery(id+"F30.imprint","IMPRINT",FACE,{"disambiguationData":[TD([[makeQuery(id+"F30.imprint","IMPRINT",EDGE,{"derivedFrom":sQuery(id+"F30.wireOp",EDGE,"E66")}),1.0]])]});
            var Q1;
            Q1=makeQuery(id+"F30.imprint","IMPRINT",FACE,{"disambiguationData":[TD([[makeQuery(id+"F30.imprint","IMPRINT",EDGE,{"derivedFrom":sQuery(id+"F30.wireOp",EDGE,"E70")}),-1.0]])]});
            extrude(context, id + "F31", {"entities" : qUnion([Q0, Q1]), "operationType" : NewBodyOperationType.REMOVE, "oppositeDirection" : true, "depth" : 25.4 * mm});
        }
        {
            var Q0;
            {var subQ0=sQuery(id+"F4.wireOp",EDGE,"E14.bottom");var subQ7=sQuery(id+"F0.wireOp",EDGE,"E0");var subQ8=sQuery(id+"F4.wireOp",EDGE,"E14.top");var subQ10=sQuery(id+"F4.wireOp",EDGE,"E14.left");Q0=makeQuery(id+"F29.boolean.opBoolean","SPLIT",FACE,{"disambiguationData":[TD([makeQuery(id+"F2.opExtrude","SWEPT_FACE",FACE,{"disambiguationData":[OSD([subQ7])]})])],"derivedFrom":makeQuery(id+"F5.opExtrude","CAP_FACE",FACE,{"disambiguationData":[OSD([subQ0,subQ8,subQ10,sQuery(id+"F4.wireOp",EDGE,"E14.right")])],"isStart":false})});}
            var sketch = newSketch(context, id + "F32", { "sketchPlane" : qUnion([Q0])});
            skLineSegment(sketch, "E74.0", {"start": v(-396.87, 314.96) * mm, "end": v(-396.87, -355.6) * mm});
            skLineSegment(sketch, "E75", {"start": v(-396.87, 314.96) * mm, "end": v(-403.22, 314.96) * mm});
            skLineSegment(sketch, "E76", {"start": v(-403.22, 314.96) * mm, "end": v(-403.23, -355.6) * mm});
            skLineSegment(sketch, "E77", {"start": v(-403.23, -355.6) * mm, "end": v(-396.87, -355.6) * mm});
            skLineSegment(sketch, "E78", {"start": v(-396.87, 314.96) * mm, "end": v(-365.12, 314.96) * mm});
            skLineSegment(sketch, "E79", {"start": v(-365.12, 314.96) * mm, "end": v(-365.12, -355.6) * mm});
            skLineSegment(sketch, "E80", {"start": v(-365.12, -355.6) * mm, "end": v(-396.87, -355.6) * mm});
            skLineSegment(sketch, "E81.MirrorCS", {"start": v(365.12, 314.96) * mm, "end": v(365.12, -355.6) * mm});
            skLineSegment(sketch, "E82.MirrorCS", {"start": v(396.87, 314.96) * mm, "end": v(396.87, -355.6) * mm});
            skLineSegment(sketch, "E83.MirrorCS", {"start": v(403.22, 314.96) * mm, "end": v(403.23, -355.6) * mm});
            skLineSegment(sketch, "E84.MirrorCS", {"start": v(396.87, 314.96) * mm, "end": v(365.12, 314.96) * mm});
            skLineSegment(sketch, "E85.MirrorCS", {"start": v(396.87, 314.96) * mm, "end": v(403.22, 314.96) * mm});
            skLineSegment(sketch, "E86.MirrorCS", {"start": v(403.23, -355.6) * mm, "end": v(396.87, -355.6) * mm});
            skLineSegment(sketch, "E87.MirrorCS", {"start": v(365.12, -355.6) * mm, "end": v(396.87, -355.6) * mm});
            skSolve(sketch);
        }
        {
            var Q0;
            Q0=makeQuery(id+"F6.imprint","IMPRINT",FACE,{"disambiguationData":[TD([[makeQuery(id+"F6.imprint","IMPRINT",EDGE,{"derivedFrom":sQuery(id+"F6.wireOp",EDGE,"E15.bottom")}),1.0]])]});
            var sketch = newSketch(context, id + "F33", { "sketchPlane" : qUnion([Q0])});
            skLineSegment(sketch, "E88", {"start": v(-920.75, 319.95) * mm, "end": v(-857.25, 319.95) * mm});
            skLineSegment(sketch, "E89", {"start": v(-857.25, 319.95) * mm, "end": v(-814.93, 361.95) * mm});
            skLineSegment(sketch, "E90.0", {"start": v(-854.63, 313.6) * mm, "end": v(-809.91, 357.99) * mm});
            skLineSegment(sketch, "E90.1", {"start": v(-920.75, 313.6) * mm, "end": v(-854.63, 313.6) * mm});
            skLineSegment(sketch, "E91", {"start": v(-920.75, 319.95) * mm, "end": v(-920.75, 313.6) * mm});
            skLineSegment(sketch, "E92", {"start": v(-814.93, 361.95) * mm, "end": v(-805.92, 361.95) * mm});
            skLineSegment(sketch, "E93", {"start": v(-809.91, 357.99) * mm, "end": v(-805.92, 361.95) * mm});
            skSolve(sketch);
        }
        {
            var Q0;
            Q0=qSketchRegion(id+"F33",true);
            var Q1;
            Q1=makeQuery(id+"F5.boolean.opBoolean","MERGE",FACE,{"derivedFrom":[makeQuery(id+"F2.opExtrude","SWEPT_FACE",FACE,{"disambiguationData":[OSD([sQuery(id+"F0.wireOp",EDGE,"E0")])]}),makeQuery(id+"F5.opExtrude","SWEPT_FACE",FACE,{"disambiguationData":[OSD([sQuery(id+"F4.wireOp",EDGE,"E14.left")])]})]});
            extrude(context, id + "F34", {"entities" : qUnion([Q0]), "operationType" : NewBodyOperationType.ADD, "endBound" : BoundingType.UP_TO_SURFACE, "oppositeDirection" : true, "endBoundEntityFace" : qUnion([Q1]), "depth" : 25.4 * mm});
        }
        {
            var Q0;
            Q0=makeQuery(id+"F32.imprint","IMPRINT",FACE,{"disambiguationData":[TD([[makeQuery(id+"F32.imprint","IMPRINT",EDGE,{"derivedFrom":sQuery(id+"F32.wireOp",EDGE,"E74.0")}),-1.0]])]});
            var Q1;
            Q1=makeQuery(id+"F32.imprint","IMPRINT",FACE,{"disambiguationData":[TD([[makeQuery(id+"F32.imprint","IMPRINT",EDGE,{"derivedFrom":sQuery(id+"F32.wireOp",EDGE,"E82.MirrorCS")}),1.0]])]});
            extrude(context, id + "F35", {"entities" : qUnion([Q0, Q1]), "oppositeDirection" : true, "depth" : 38.1 * mm});
        }
        {
            var Q0;
            Q0=makeQuery(id+"F32.imprint","IMPRINT",FACE,{"disambiguationData":[TD([[makeQuery(id+"F32.imprint","IMPRINT",EDGE,{"derivedFrom":sQuery(id+"F32.wireOp",EDGE,"E74.0")}),1.0]])]});
            var Q1;
            Q1=makeQuery(id+"F32.imprint","IMPRINT",FACE,{"disambiguationData":[TD([[makeQuery(id+"F32.imprint","IMPRINT",EDGE,{"derivedFrom":sQuery(id+"F32.wireOp",EDGE,"E81.MirrorCS")}),1.0]])]});
            extrude(context, id + "F36", {"entities" : qUnion([Q0, Q1]), "oppositeDirection" : true, "depth" : 6.35 * mm});
        }
        {
            var Q0;
            {var subQ0=sQuery(id+"F0.wireOp",EDGE,"E3");Q0=makeQuery(id+"F5.boolean.opBoolean","MERGE",FACE,{"derivedFrom":[makeQuery(id+"F3.boolean.opBoolean","MERGE",FACE,{"derivedFrom":[makeQuery(id+"F2.opExtrude","SWEPT_FACE",FACE,{"disambiguationData":[OSD([subQ0]),TDD([makeQuery(id+"F0.imprint","IMPRINT",EDGE,{"disambiguationData":[TD([[makeQuery(id+"F0.imprint","INTERSECT",VERTEX,{"derivedFrom":[sQuery(id+"F0.wireOp",EDGE,"E0"),subQ0]}),-1.0]])],"derivedFrom":subQ0})])]}),makeQuery(id+"F2.opExtrude","SWEPT_FACE",FACE,{"disambiguationData":[OSD([subQ0]),TDD([makeQuery(id+"F0.imprint","IMPRINT",EDGE,{"disambiguationData":[TD([[makeQuery(id+"F0.imprint","INTERSECT",VERTEX,{"derivedFrom":[sQuery(id+"F0.wireOp",EDGE,"E2"),subQ0]}),1.0]])],"derivedFrom":subQ0})])]}),makeQuery(id+"F3.opExtrude","SWEPT_FACE",FACE,{"disambiguationData":[OSD([subQ0])]})]}),makeQuery(id+"F5.opExtrude","SWEPT_FACE",FACE,{"disambiguationData":[OSD([sQuery(id+"F4.wireOp",EDGE,"E14.bottom")])]})]});}
            var sketch = newSketch(context, id + "F37", { "sketchPlane" : qUnion([Q0])});
            skCircle(sketch, "E94", {"center": v(0, -460.38) * mm, "radius": 30.8 * mm});
            skLineSegment(sketch, "E95", {"start": v(-558.8, -460.38) * mm, "end": v(558.8, -460.38) * mm});
            skLineSegment(sketch, "E96", {"start": v(-558.8, 0) * mm, "end": v(558.8, -920.75) * mm});
            skLineSegment(sketch, "E97", {"start": v(558.8, 0) * mm, "end": v(-558.8, -920.75) * mm});
            skLineSegment(sketch, "E98.0", {"start": v(-655.7, -117.62) * mm, "end": v(461.9, -1038.37) * mm});
            skLineSegment(sketch, "E99.0", {"start": v(-849.52, -352.87) * mm, "end": v(268.08, -1273.62) * mm});
            skLineSegment(sketch, "E100.MirrorCS", {"start": v(-461.9, 117.62) * mm, "end": v(655.7, -803.13) * mm});
            skLineSegment(sketch, "E101.MirrorCS", {"start": v(-364.99, 235.25) * mm, "end": v(752.61, -685.5) * mm});
            skLineSegment(sketch, "E102.MirrorCS", {"start": v(-268.08, 352.87) * mm, "end": v(849.52, -567.88) * mm});
            skCircle(sketch, "E103", {"center": v(-239.68, -460.38) * mm, "radius": 27.46 * mm});
            skCircle(sketch, "E104", {"center": v(0, -262.92) * mm, "radius": 30.52 * mm});
            skCircle(sketch, "E105", {"center": v(239.68, -460.38) * mm, "radius": 25.3 * mm});
            skCircle(sketch, "E106", {"center": v(0, -657.83) * mm, "radius": 36 * mm});
            skCircle(sketch, "E107", {"center": v(0, -65.46) * mm, "radius": 22.27 * mm});
            skCircle(sketch, "E108", {"center": v(0, -855.3) * mm, "radius": 7.94 * mm});
            skCircle(sketch, "E109", {"center": v(-239.68, -657.83) * mm, "radius": 23.61 * mm});
            skCircle(sketch, "E110", {"center": v(-359.51, -756.56) * mm, "radius": 25.7 * mm});
            skCircle(sketch, "E111", {"center": v(-475.54, -460.38) * mm, "radius": 27.07 * mm});
            skCircle(sketch, "E112", {"center": v(479.35, -460.38) * mm, "radius": 21.84 * mm});
            skCircle(sketch, "E113", {"center": v(-119.84, -559.1) * mm, "radius": 23.59 * mm});
            skCircle(sketch, "E114.MirrorC", {"center": v(119.84, -559.1) * mm, "radius": 23.59 * mm});
            skCircle(sketch, "E115.MirrorC", {"center": v(239.68, -657.83) * mm, "radius": 23.61 * mm});
            skCircle(sketch, "E116.MirrorC", {"center": v(359.51, -756.56) * mm, "radius": 25.7 * mm});
            skCircle(sketch, "E117.MirrorC", {"center": v(-239.68, -262.92) * mm, "radius": 23.61 * mm});
            skLineSegment(sketch, "E118.MirrorCS", {"start": v(558.8, -920.75) * mm, "end": v(-558.8, 0) * mm});
            skCircle(sketch, "E119.MirrorC", {"center": v(-119.84, -361.65) * mm, "radius": 23.59 * mm});
            skCircle(sketch, "E120.MirrorC", {"center": v(-359.51, -164.19) * mm, "radius": 25.7 * mm});
            skCircle(sketch, "E121.MirrorC", {"center": v(119.84, -361.65) * mm, "radius": 23.59 * mm});
            skSolve(sketch);
        }
        {
            var Q0;
            Q0=sQuery(id+"F37.wireOp",VERTEX,"E103.center");
            var Q1;
            Q1=sQuery(id+"F37.wireOp",VERTEX,"E111.center");
            var Q2;
            Q2=sQuery(id+"F37.wireOp",VERTEX,"E104.center");
            var Q3;
            Q3=sQuery(id+"F37.wireOp",VERTEX,"E107.center");
            var Q4;
            Q4=sQuery(id+"F37.wireOp",VERTEX,"E121.MirrorC.center");
            var Q5;
            Q5=sQuery(id+"F37.wireOp",VERTEX,"E105.center");
            var Q6;
            Q6=sQuery(id+"F37.wireOp",VERTEX,"E112.center");
            var Q7;
            Q7=sQuery(id+"F37.wireOp",VERTEX,"E115.MirrorC.center");
            var Q8;
            Q8=sQuery(id+"F37.wireOp",VERTEX,"E114.MirrorC.center");
            var Q9;
            Q9=sQuery(id+"F37.wireOp",VERTEX,"E116.MirrorC.center");
            var Q10;
            Q10=sQuery(id+"F37.wireOp",VERTEX,"E106.center");
            var Q11;
            Q11=sQuery(id+"F37.wireOp",VERTEX,"E113.center");
            var Q12;
            Q12=sQuery(id+"F37.wireOp",VERTEX,"E109.center");
            var Q13;
            Q13=sQuery(id+"F37.wireOp",VERTEX,"E110.center");
            var Q14;
            Q14=sQuery(id+"F37.wireOp",VERTEX,"E119.MirrorC.center");
            var Q15;
            Q15=sQuery(id+"F37.wireOp",VERTEX,"E117.MirrorC.center");
            var Q16;
            Q16=sQuery(id+"F37.wireOp",VERTEX,"E120.MirrorC.center");
            var Q17;
            Q17=makeQuery(id+"F36.opExtrude","SWEPT_BODY",BODY,{"disambiguationData":[OSD([sQuery(id+"F32.wireOp",EDGE,"E74.0"),sQuery(id+"F32.wireOp",EDGE,"E78"),sQuery(id+"F32.wireOp",EDGE,"E79"),sQuery(id+"F32.wireOp",EDGE,"E80")])]});
            hole(context, id + "F38", {"style" : HoleStyle.SIMPLE, "endStyle" : HoleEndStyle.BLIND, "holeDiameter" : 25.4 * mm, "holeDepth" : 50.8 * mm, "locations" : qUnion([Q0, Q1, Q2, Q3, Q4, Q5, Q6, Q7, Q8, Q9, Q10, Q11, Q12, Q13, Q14, Q15, Q16]), "scope" : qUnion([Q17])});
        }
        {
            var Q0;
            Q0=sQuery(id+"F37.wireOp",VERTEX,"E94.center");
            var Q1;
            Q1=makeQuery(id+"F36.opExtrude","SWEPT_BODY",BODY,{"disambiguationData":[OSD([sQuery(id+"F32.wireOp",EDGE,"E74.0"),sQuery(id+"F32.wireOp",EDGE,"E78"),sQuery(id+"F32.wireOp",EDGE,"E79"),sQuery(id+"F32.wireOp",EDGE,"E80")])]});
            hole(context, id + "F39", {"style" : HoleStyle.SIMPLE, "endStyle" : HoleEndStyle.BLIND, "holeDiameter" : 38.1 * mm, "holeDepth" : 50.8 * mm, "locations" : qUnion([Q0]), "scope" : qUnion([Q1])});
        }
        {
            var Q0;
            Q0=makeQuery(id+"F37.imprint","IMPRINT",FACE,{"disambiguationData":[TD([[makeQuery(id+"F37.imprint","IMPRINT",EDGE,{"derivedFrom":sQuery(id+"F37.wireOp",EDGE,"E108")}),1.0]])]});
            extrude(context, id + "F40", {"entities" : qUnion([Q0]), "operationType" : NewBodyOperationType.ADD, "depth" : 34.92 * mm});
        }
        {
            var Q0;
            {var subQ0=sQuery(id+"F11.wireOp",EDGE,"E23");Q0=makeQuery(id+"F11.imprint","IMPRINT",FACE,{"disambiguationData":[TD([[makeQuery(id+"F11.imprint","IMPRINT",EDGE,{"derivedFrom":subQ0}),1.0]])]});}
            extrude(context, id + "F41", {"entities" : qUnion([Q0]), "operationType" : NewBodyOperationType.REMOVE, "oppositeDirection" : true, "depth" : 1270 * mm});
        }
        {
            var Q0;
            {var subQ1=sQuery(id+"F0.wireOp",EDGE,"E11");var subQ2=sQuery(id+"F21.wireOp",EDGE,"E44.MirrorCS");Q0=makeQuery(id+"F24.opBoolean","SPLIT",FACE,{"disambiguationData":[TD([makeQuery(id+"F3.opExtrude","SWEPT_FACE",FACE,{"disambiguationData":[OSD([sQuery(id+"F0.wireOp",EDGE,"E5"),sQuery(id+"F0.wireOp",EDGE,"E10"),subQ1])]})])],"derivedFrom":makeQuery(id+"F23.opExtrude","SWEPT_FACE",FACE,{"disambiguationData":[OSD([subQ2])]})});}
            extrude(context, id + "F42", {"entities" : qUnion([Q0]), "operationType" : NewBodyOperationType.REMOVE, "oppositeDirection" : true, "depth" : 889 * mm});
        }
        {
            var Q0;
            Q0=makeQuery(id+"F41.boolean.opBoolean","COPY",FACE,{"derivedFrom":makeQuery(id+"F41.opExtrude","SWEPT_FACE",FACE,{"disambiguationData":[OSD([sQuery(id+"F11.wireOp",EDGE,"E27")])]})});
            var sketch = newSketch(context, id + "F43", { "sketchPlane" : qUnion([Q0])});
            skLineSegment(sketch, "E122", {"start": v(-558.8, -361.95) * mm, "end": v(-558.8, -355.6) * mm});
            skLineSegment(sketch, "E123", {"start": v(-558.8, -355.6) * mm, "end": v(558.8, -355.6) * mm});
            skLineSegment(sketch, "E124", {"start": v(558.8, -355.6) * mm, "end": v(558.8, -361.95) * mm});
            skLineSegment(sketch, "E125", {"start": v(558.8, -361.95) * mm, "end": v(-558.8, -361.95) * mm});
            skSolve(sketch);
        }
        {
            var Q0;
            Q0 = qSketchRegion(id + "F43", true);
            extrude(context, id + "F44", {"entities" : qUnion([Q0]), "operationType" : NewBodyOperationType.ADD, "depth" : 76.2 * mm});
        }
        {
            var Q0;
            Q0=makeQuery(id+"F44.opExtrude","CAP_EDGE",EDGE,{"disambiguationData":[OSD([sQuery(id+"F43.wireOp",EDGE,"E122")])],"isStart":false});
            var Q1;
            Q1=makeQuery(id+"F44.opExtrude","CAP_EDGE",EDGE,{"disambiguationData":[OSD([sQuery(id+"F43.wireOp",EDGE,"E124")])],"isStart":false});
            chamfer(context, id + "F45", {"entities" : qUnion([Q0, Q1]), "width" : 50.8 * mm, "tangentPropagation" : true});
        }
        {
            var Q0;
            {var subQ0=sQuery(id+"F0.wireOp",EDGE,"E7");Q0=makeQuery(id+"F44.boolean.opBoolean","MERGE",FACE,{"derivedFrom":[makeQuery(id+"F42.boolean.opBoolean","MERGE",FACE,{"derivedFrom":[makeQuery(id+"F20.boolean.opBoolean","MERGE",FACE,{"derivedFrom":[makeQuery(id+"F3.opExtrude","SWEPT_FACE",FACE,{"disambiguationData":[OSD([subQ0,sQuery(id+"F0.wireOp",EDGE,"E12"),sQuery(id+"F0.wireOp",EDGE,"E13")])]}),makeQuery(id+"F20.opExtrude","SWEPT_FACE",FACE,{"disambiguationData":[OSD([subQ0])]})]}),makeQuery(id+"F42.opExtrude","SWEPT_FACE",FACE,{"disambiguationData":[OSD([sQuery(id+"F21.wireOp",EDGE,"E44.MirrorCS"),sQuery(id+"F21.wireOp",EDGE,"E46.MirrorCS"),sQuery(id+"F21.wireOp",EDGE,"E52.MirrorCS")])]})]}),makeQuery(id+"F44.opExtrude","SWEPT_FACE",FACE,{"disambiguationData":[OSD([sQuery(id+"F43.wireOp",EDGE,"E123")])]})]});}
            var sketch = newSketch(context, id + "F46", { "sketchPlane" : qUnion([Q0])});
            skLineSegment(sketch, "E126", {"start": v(-558.8, 19.05) * mm, "end": v(558.8, 19.05) * mm});
            skLineSegment(sketch, "E127", {"start": v(-558.8, 19.05) * mm, "end": v(-457.2, 19.05) * mm});
            skLineSegment(sketch, "E128", {"start": v(-457.2, 69.85) * mm, "end": v(-457.2, 44.45) * mm});
            skCircle(sketch, "E129", {"center": v(-457.2, 44.45) * mm, "radius": 7.94 * mm});
            skCircle(sketch, "E130.MirrorC", {"center": v(457.2, 44.45) * mm, "radius": 7.94 * mm});
            skSolve(sketch);
        }
        {
            var Q0;
            Q0=makeQuery(id+"F46.imprint","IMPRINT",FACE,{"disambiguationData":[TD([[makeQuery(id+"F46.imprint","IMPRINT",EDGE,{"derivedFrom":sQuery(id+"F46.wireOp",EDGE,"E129")}),1.0]])]});
            var Q1;
            Q1=makeQuery(id+"F46.imprint","IMPRINT",FACE,{"disambiguationData":[TD([[makeQuery(id+"F46.imprint","IMPRINT",EDGE,{"derivedFrom":sQuery(id+"F46.wireOp",EDGE,"E130.MirrorC")}),-1.0]])]});
            extrude(context, id + "F47", {"entities" : qUnion([Q0, Q1]), "operationType" : NewBodyOperationType.REMOVE, "oppositeDirection" : true, "depth" : 44.45 * mm});
        }
        {
            var Q0;
            Q0=makeQuery(id+"F26.opExtrude","SWEPT_BODY",BODY,{"disambiguationData":[OSD([sQuery(id+"F21.wireOp",EDGE,"E38.0"),sQuery(id+"F21.wireOp",EDGE,"E41.0"),sQuery(id+"F21.wireOp",EDGE,"E42.MirrorCS"),sQuery(id+"F21.wireOp",EDGE,"E43.MirrorCS"),sQuery(id+"F21.wireOp",EDGE,"E47"),sQuery(id+"F21.wireOp",EDGE,"E48"),sQuery(id+"F21.wireOp",EDGE,"E49"),sQuery(id+"F21.wireOp",EDGE,"E50.MirrorCS"),sQuery(id+"F21.wireOp",EDGE,"E51.MirrorCS"),sQuery(id+"F25.wireOp",EDGE,"E53.0"),sQuery(id+"F25.wireOp",EDGE,"E53.1"),sQuery(id+"F25.wireOp",EDGE,"E53.2"),sQuery(id+"F25.wireOp",EDGE,"E54.MirrorCS"),sQuery(id+"F25.wireOp",EDGE,"E55.0"),sQuery(id+"F25.wireOp",EDGE,"E55.1"),sQuery(id+"F25.wireOp",EDGE,"E55.2"),sQuery(id+"F25.wireOp",EDGE,"E56")])]});
            var Q1;
            Q1=makeQuery(id+"F41.boolean.opBoolean","SPLIT",BODY,{"disambiguationData":[OD(0.0)],"derivedFrom":makeQuery(id+"F36.opExtrude","SWEPT_BODY",BODY,{"disambiguationData":[OSD([sQuery(id+"F32.wireOp",EDGE,"E74.0"),sQuery(id+"F32.wireOp",EDGE,"E78"),sQuery(id+"F32.wireOp",EDGE,"E79"),sQuery(id+"F32.wireOp",EDGE,"E80")])]})});
            var Q2;
            Q2=makeQuery(id+"F41.boolean.opBoolean","SPLIT",BODY,{"disambiguationData":[OD(1.0)],"derivedFrom":makeQuery(id+"F36.opExtrude","SWEPT_BODY",BODY,{"disambiguationData":[OSD([sQuery(id+"F32.wireOp",EDGE,"E74.0"),sQuery(id+"F32.wireOp",EDGE,"E78"),sQuery(id+"F32.wireOp",EDGE,"E79"),sQuery(id+"F32.wireOp",EDGE,"E80")])]})});
            deleteBodies(context, id + "F48", {"entities" : qUnion([Q0, Q1, Q2])});
        }
        {
            var Q0;
            Q0=makeQuery(id+"F44.boolean.opBoolean","MERGE",FACE,{"derivedFrom":[makeQuery(id+"F5.boolean.opBoolean","MERGE",FACE,{"derivedFrom":[makeQuery(id+"F2.opExtrude","SWEPT_FACE",FACE,{"disambiguationData":[OSD([sQuery(id+"F0.wireOp",EDGE,"E2")])]}),makeQuery(id+"F5.opExtrude","SWEPT_FACE",FACE,{"disambiguationData":[OSD([sQuery(id+"F4.wireOp",EDGE,"E14.right")])]})]}),makeQuery(id+"F44.opExtrude","SWEPT_FACE",FACE,{"disambiguationData":[OSD([sQuery(id+"F43.wireOp",EDGE,"E122")])]})]});
            var sketch = newSketch(context, id + "F49", { "sketchPlane" : qUnion([Q0])});
            skLineSegment(sketch, "E131", {"start": v(-685.8, 361.95) * mm, "end": v(-768.35, 361.95) * mm});
            skLineSegment(sketch, "E132", {"start": v(-768.35, 361.95) * mm, "end": v(-6.35, -355.6) * mm});
            skLineSegment(sketch, "E133", {"start": v(-6.35, -355.6) * mm, "end": v(-6.35, -279.75) * mm});
            skLineSegment(sketch, "E134", {"start": v(-6.35, -279.75) * mm, "end": v(-685.8, 361.95) * mm});
            skSolve(sketch);
        }
        {
            var Q0;
            Q0=makeQuery(id+"F49.imprint","IMPRINT",FACE,{"disambiguationData":[TD([[makeQuery(id+"F49.imprint","IMPRINT",EDGE,{"derivedFrom":sQuery(id+"F49.wireOp",EDGE,"E131")}),-1.0]])]});
            extrude(context, id + "F50", {"entities" : qUnion([Q0]), "depth" : 3.17 * mm});
        }
        {
            var Q0;
            Q0 = qSketchRegion(id + "F49", true);
            var Q1;
            {var subQ0=sQuery(id+"F6.wireOp",EDGE,"E16.0");var subQ2=sQuery(id+"F0.wireOp",EDGE,"E9");var subQ3=makeQuery(id+"F2.opExtrude","SWEPT_FACE",FACE,{"disambiguationData":[OSD([subQ2])]});Q1=makeQuery(id+"F34.boolean.opBoolean","SPLIT",FACE,{"disambiguationData":[TD([makeQuery(id+"F8.opExtrude","SWEPT_FACE",FACE,{"disambiguationData":[OSD([subQ0])]})])],"derivedFrom":subQ3});}
            extrude(context, id + "F51", {"entities" : qUnion([Q0]), "oppositeDirection" : true, "depth" : 9.52 * mm, "hasSecondDirection" : true, "secondDirectionBound" : SecondDirectionBoundingType.UP_TO_SURFACE, "secondDirectionOppositeDirection" : true, "secondDirectionBoundEntityFace" : qUnion([Q1]), "secondDirectionDepth" : 8.9 * mm});
        }
        {
            var Q0;
            Q0=makeQuery(id+"F50.opExtrude","SWEPT_BODY",BODY,{"disambiguationData":[OSD([sQuery(id+"F49.wireOp",EDGE,"E131"),sQuery(id+"F49.wireOp",EDGE,"E132"),sQuery(id+"F49.wireOp",EDGE,"E133"),sQuery(id+"F49.wireOp",EDGE,"E134")])]});
            var Q1;
            Q1=makeQuery(id+"F51.opExtrude","SWEPT_BODY",BODY,{"disambiguationData":[OSD([sQuery(id+"F49.wireOp",EDGE,"E131"),sQuery(id+"F49.wireOp",EDGE,"E132"),sQuery(id+"F49.wireOp",EDGE,"E133"),sQuery(id+"F49.wireOp",EDGE,"E134")])]});
            var Q2;
            Q2=qCreatedBy(makeId("Right.planeOp"),FACE);
            mirror(context, id + "F52", {"entities" : qUnion([Q0, Q1]), "mirrorPlane" : qUnion([Q2])});
        }
        {
            var Q0;
            Q0=makeQuery(id+"F40.opExtrude","CAP_FACE",FACE,{"disambiguationData":[OSD([sQuery(id+"F37.wireOp",EDGE,"E108")])],"isStart":false});
            extrude(context, id + "F53", {"entities" : qUnion([Q0]), "operationType" : NewBodyOperationType.REMOVE, "oppositeDirection" : true, "depth" : 34.92 * mm});
        }
    });
